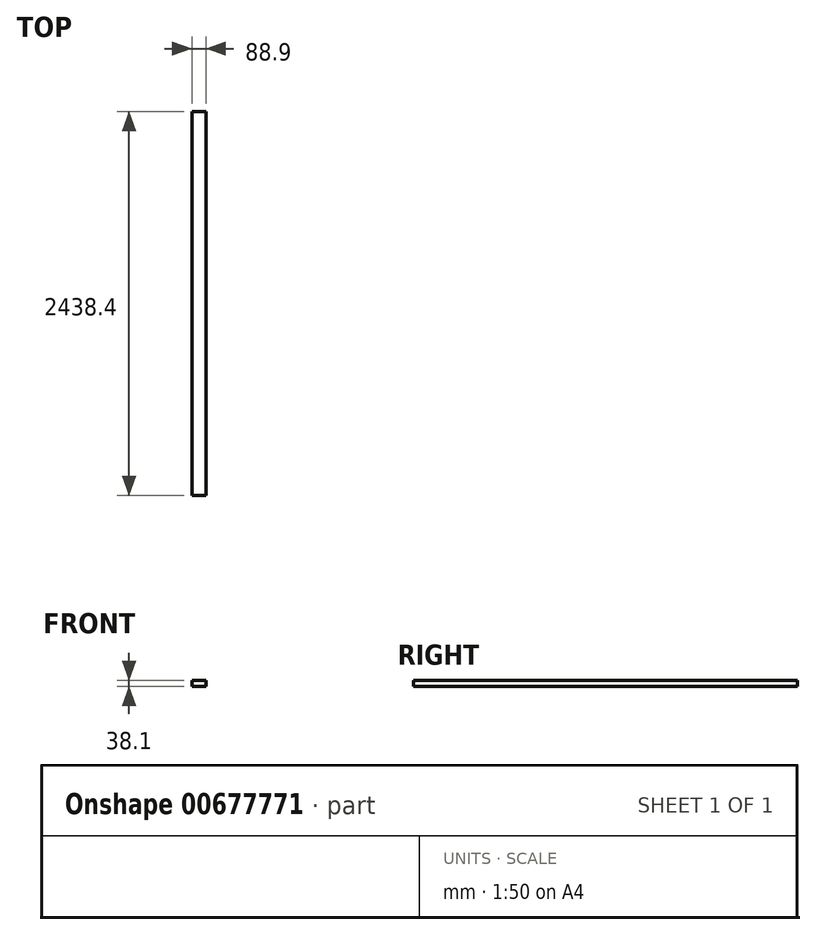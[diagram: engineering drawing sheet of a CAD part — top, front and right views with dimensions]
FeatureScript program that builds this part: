
annotation { "Feature Type Name" : "Feature", "Feature Type Description" : "" }
export const myFeature = defineFeature(function(context is Context, id is Id, definition is map)
    precondition{}
    {
        {
            var Q0;
            Q0=qCreatedBy(makeId("Front.planeOp"),FACE);
            var sketch = newSketch(context, id + "F0", { "sketchPlane" : qUnion([Q0])});
            skLineSegment(sketch, "E0.bottom", {"start": v(44.45, 19.05) * mm, "end": v(-44.45, 19.05) * mm});
            skLineSegment(sketch, "E0.top", {"start": v(44.45, -19.05) * mm, "end": v(-44.45, -19.05) * mm});
            skLineSegment(sketch, "E0.left", {"start": v(44.45, 19.05) * mm, "end": v(44.45, -19.05) * mm});
            skLineSegment(sketch, "E0.right", {"start": v(-44.45, 19.05) * mm, "end": v(-44.45, -19.05) * mm});
            skPoint(sketch, "E0.middle", {"position": v(0, 0) * mm});
            skSolve(sketch);
        }
        {
            var Q0;
            Q0 = qSketchRegion(id + "F0", true);
            extrude(context, id + "F1", {"entities" : qUnion([Q0]), "depth" : 2438.4 * mm, "offsetDistance" : 25.4 * mm});
        }
    });
